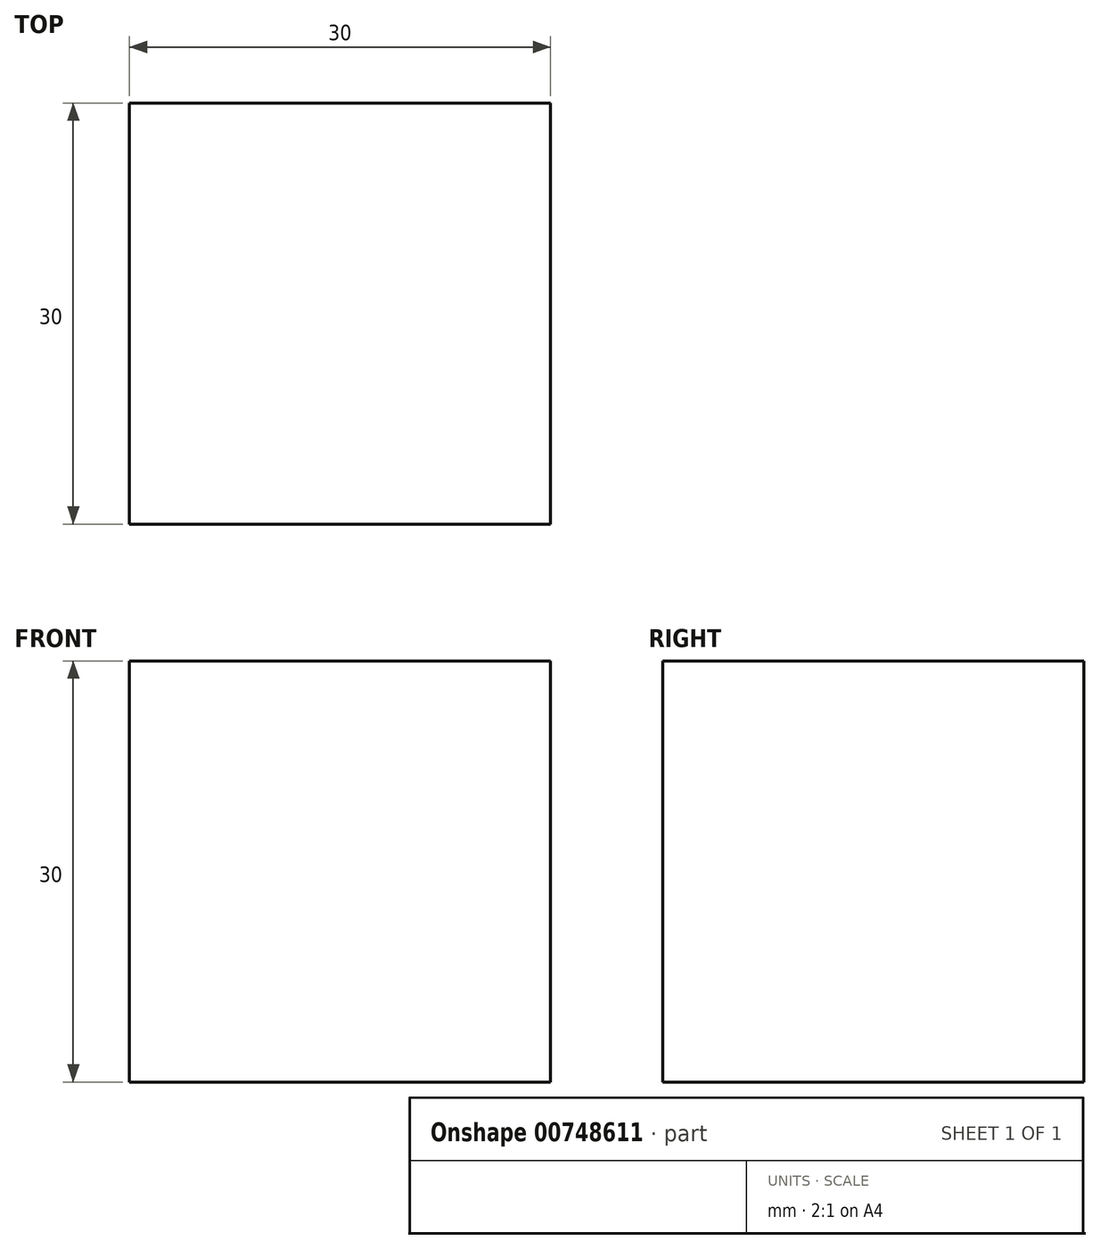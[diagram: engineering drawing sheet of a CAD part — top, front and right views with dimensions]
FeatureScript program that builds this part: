
annotation { "Feature Type Name" : "Feature", "Feature Type Description" : "" }
export const myFeature = defineFeature(function(context is Context, id is Id, definition is map)
    precondition{}
    {
        {
            var Q0;
            Q0=qCreatedBy(makeId("Top.planeOp"),FACE);
            var sketch = newSketch(context, id + "F0", { "sketchPlane" : qUnion([Q0])});
            skLineSegment(sketch, "E0.bottom", {"start": v(-20.54, 48.12) * mm, "end": v(9.46, 48.12) * mm});
            skLineSegment(sketch, "E0.top", {"start": v(-20.54, 18.12) * mm, "end": v(9.46, 18.12) * mm});
            skLineSegment(sketch, "E0.left", {"start": v(-20.54, 48.12) * mm, "end": v(-20.54, 18.12) * mm});
            skLineSegment(sketch, "E0.right", {"start": v(9.46, 48.12) * mm, "end": v(9.46, 18.12) * mm});
            skSolve(sketch);
        }
        {
            var Q0;
            Q0 = qSketchRegion(id + "F0", true);
            extrude(context, id + "F1", {"entities" : qUnion([Q0]), "depth" : 30 * mm, "offsetDistance" : 25 * mm});
        }
    });
